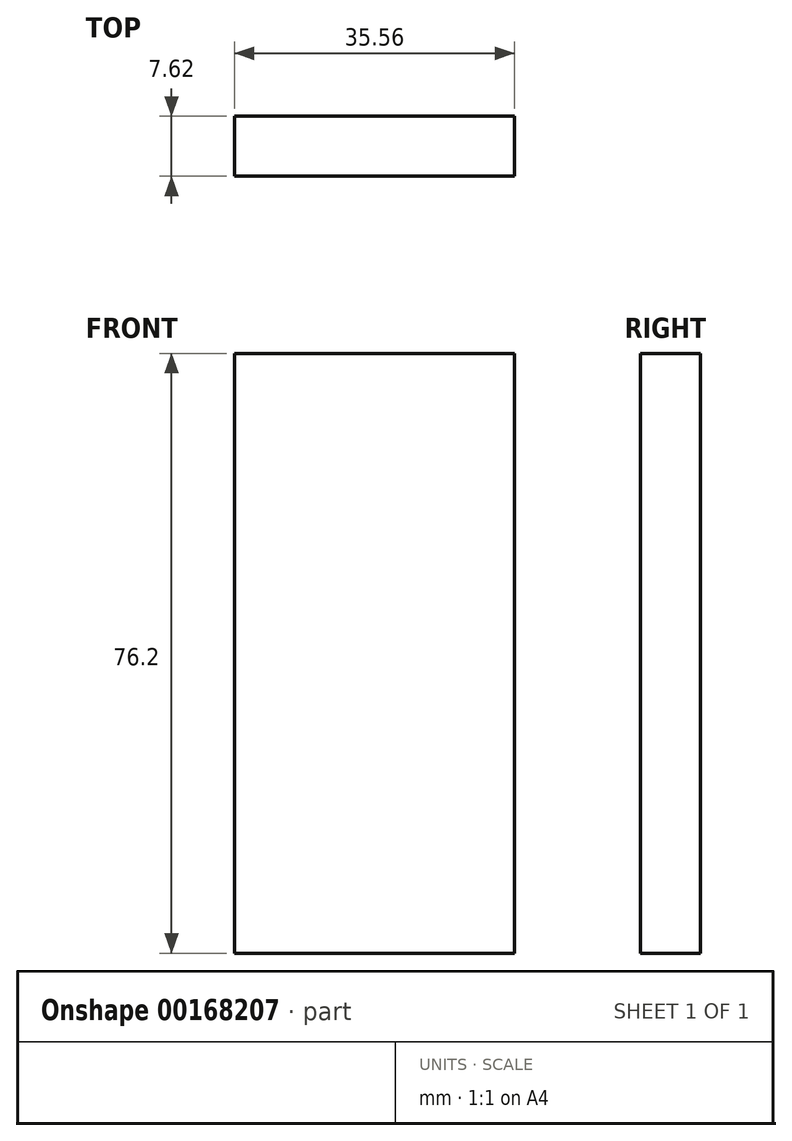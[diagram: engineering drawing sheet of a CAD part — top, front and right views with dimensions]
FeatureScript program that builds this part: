
annotation { "Feature Type Name" : "Feature", "Feature Type Description" : "" }
export const myFeature = defineFeature(function(context is Context, id is Id, definition is map)
    precondition{}
    {
        {
            var Q0;
            Q0=qCreatedBy(makeId("Front.planeOp"),FACE);
            var sketch = newSketch(context, id + "F0", { "sketchPlane" : qUnion([Q0])});
            skLineSegment(sketch, "E0.bottom", {"start": v(17.78, -38.1) * mm, "end": v(-17.78, -38.1) * mm});
            skLineSegment(sketch, "E0.top", {"start": v(17.78, 38.1) * mm, "end": v(-17.78, 38.1) * mm});
            skLineSegment(sketch, "E0.left", {"start": v(17.78, -38.1) * mm, "end": v(17.78, 38.1) * mm});
            skLineSegment(sketch, "E0.right", {"start": v(-17.78, -38.1) * mm, "end": v(-17.78, 38.1) * mm});
            skPoint(sketch, "E0.middle", {"position": v(0, 0) * mm});
            skSolve(sketch);
        }
        {
            var Q0;
            Q0 = qSketchRegion(id + "F0", true);
            extrude(context, id + "F1", {"entities" : qUnion([Q0]), "depth" : 7.62 * mm});
        }
    });
